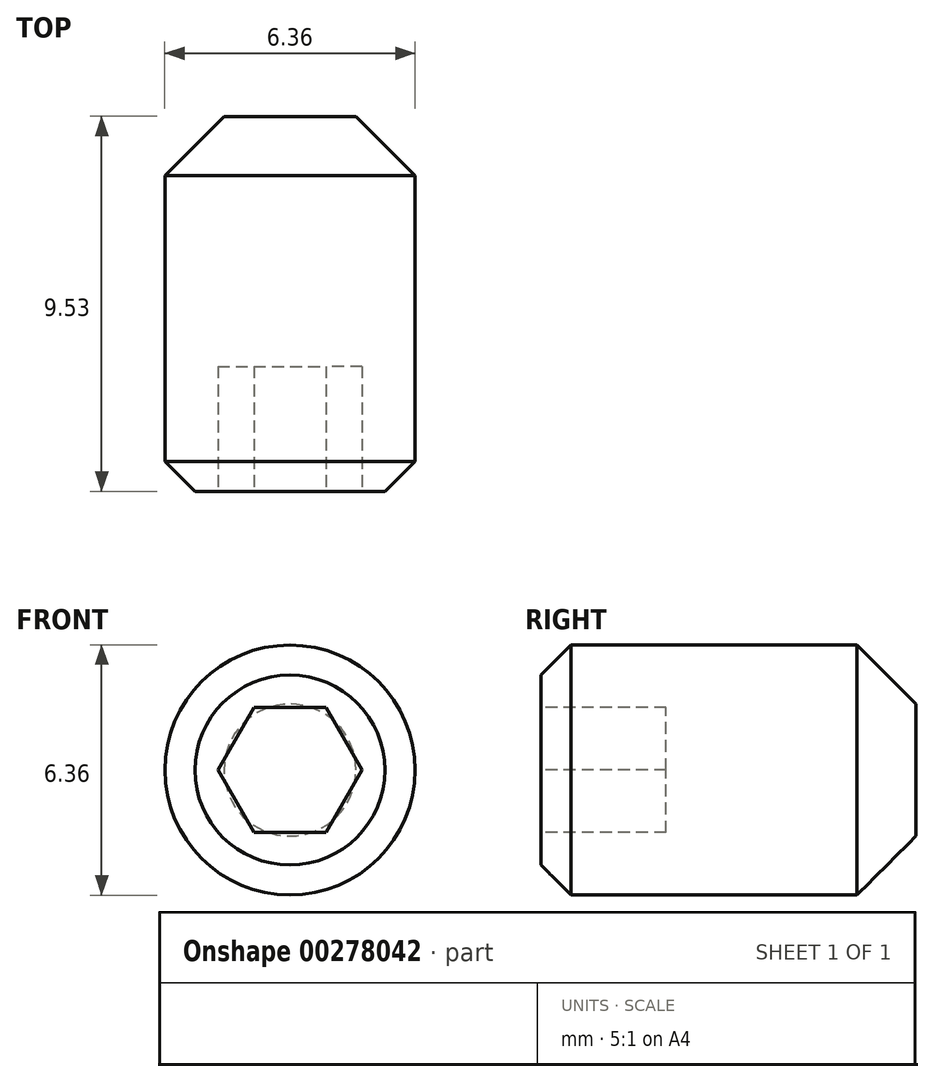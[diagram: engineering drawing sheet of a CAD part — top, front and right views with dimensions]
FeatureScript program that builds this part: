
annotation { "Feature Type Name" : "Feature", "Feature Type Description" : "" }
export const myFeature = defineFeature(function(context is Context, id is Id, definition is map)
    precondition{}
    {
        {
            var Q0;
            Q0=qCreatedBy(makeId("Front.planeOp"),FACE);
            var sketch = newSketch(context, id + "F0", { "sketchPlane" : qUnion([Q0])});
            skCircle(sketch, "E0", {"center": v(0, 0) * mm, "radius": 3.18 * mm});
            skSolve(sketch);
        }
        {
            var Q0;
            Q0=makeQuery(id+"F0.imprint","IMPRINT",FACE,{"disambiguationData":[TD([[makeQuery(id+"F0.imprint","IMPRINT",EDGE,{"derivedFrom":sQuery(id+"F0.wireOp",EDGE,"E0")}),1.0]])]});
            extrude(context, id + "F1", {"entities" : qUnion([Q0]), "oppositeDirection" : true, "depth" : 9.52 * mm});
        }
        {
            var Q0;
            Q0=makeQuery(id+"F1.opExtrude","CAP_EDGE",EDGE,{"disambiguationData":[OSD([sQuery(id+"F0.wireOp",EDGE,"E0")])],"isStart":false});
            chamfer(context, id + "F2", {"entities" : qUnion([Q0]), "chamferType" : ChamferType.OFFSET_ANGLE, "width" : 1.5 * mm, "oppositeDirection" : false, "angle" : 45 * degree, "tangentPropagation" : true});
        }
        {
            var Q0;
            Q0=makeQuery(id+"F1.opExtrude","CAP_EDGE",EDGE,{"disambiguationData":[OSD([sQuery(id+"F0.wireOp",EDGE,"E0")])],"isStart":true});
            chamfer(context, id + "F3", {"entities" : qUnion([Q0]), "chamferType" : ChamferType.OFFSET_ANGLE, "width" : 0.76 * mm, "oppositeDirection" : false, "angle" : 45 * degree, "tangentPropagation" : true});
        }
        {
            var Q0;
            Q0=makeQuery(id+"F1.opExtrude","CAP_FACE",FACE,{"disambiguationData":[OSD([sQuery(id+"F0.wireOp",EDGE,"E0")])],"isStart":true});
            var sketch = newSketch(context, id + "F4", { "sketchPlane" : qUnion([Q0])});
            skCircle(sketch, "E1.cCircle", {"center": v(0, 0) * mm, "radius": 1.59 * mm, "construction": true});
            skLineSegment(sketch, "E1.0", {"start": v(-0.92, 1.59) * mm, "end": v(0.92, 1.59) * mm});
            skLineSegment(sketch, "E1.1", {"start": v(0.92, 1.59) * mm, "end": v(1.83, 0) * mm});
            skLineSegment(sketch, "E1.2", {"start": v(1.83, 0) * mm, "end": v(0.92, -1.59) * mm});
            skLineSegment(sketch, "E1.3", {"start": v(0.92, -1.59) * mm, "end": v(-0.92, -1.59) * mm});
            skLineSegment(sketch, "E1.4", {"start": v(-0.92, -1.59) * mm, "end": v(-1.83, 0) * mm});
            skLineSegment(sketch, "E1.5", {"start": v(-1.83, 0) * mm, "end": v(-0.92, 1.59) * mm});
            skPoint(sketch, "E1.0.midPoint", {"position": v(0, 1.59) * mm});
            skSolve(sketch);
        }
        {
            var Q0;
            Q0=makeQuery(id+"F4.imprint","IMPRINT",FACE,{"disambiguationData":[TD([[makeQuery(id+"F4.imprint","IMPRINT",EDGE,{"derivedFrom":sQuery(id+"F4.wireOp",EDGE,"E1.0")}),-1.0]])]});
            extrude(context, id + "F5", {"entities" : qUnion([Q0]), "operationType" : NewBodyOperationType.REMOVE, "oppositeDirection" : true, "depth" : 3.17 * mm});
        }
    });
